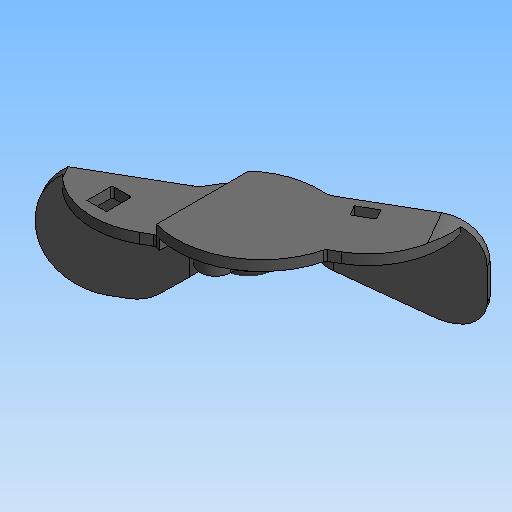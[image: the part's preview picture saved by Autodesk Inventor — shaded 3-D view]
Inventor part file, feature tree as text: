
AUTODESK INVENTOR PART (.ipt)
format: ipt  version: 2020 (Build 240168000, 168)  size: 249,344 bytes
history: native  units: mm (DEFAULTED — no unit token found)
features: sketch x7, other x7, extrude x6, revolve x1
ambient origin geometry x8: Origin, YZ Plane, XZ Plane, XY Plane, X Axis, Y Axis, Z Axis, Center Point
bodies: Solid1 (feature_tree)
feature tree (21):
  extrude  "Extrusion1"  Depth=50.0mm TaperAngle=0.0deg
  extrude  "Extrusion2"  Depth=2.3mm TaperAngle=0.0deg
  extrude  "Extrusion3"  Depth=2.7mm TaperAngle=0.0deg
  extrude  "Extrusion4"  TaperAngle=0.0deg  [1 undecoded]
  extrude  "Extrusion5"  [1 undecoded]
  sketch  "Sketch_7"
  extrude  "Extrusion6"  [1 undecoded]
  revolve  "Revolution1"  [1 undecoded]
  other  "stopper_to_body_XY"
  other  "stopper_to_body_YZ"
  other  "stopper_to_body_ZX"
  other  "stopper_to_body_X"
  other  "stopper_to_body_Y"
  other  "stopper_to_body_Z"
  other  "stopper_to_body_Center"
  sketch  "Sketch_1"  dims[d0=25.0mm d1=0.0mm d2=50.0mm d3=0.0mm]
  sketch  "Sketch_2"  dims[d4=50.0mm d5=0.0mm d6=2.3mm d7=0.0mm]
  sketch  "Sketch_8"
  sketch  "Sketch_9"
  sketch  "Sketch_3"  dims[d8=100.0mm d9=0.0mm d10=2.7mm d11=0.0mm]
  sketch  "Sketch_4"  dims[d12=360.0deg d13=0.0mm]
note: 4 required parameter values undecoded (feature->parameter linkage not recoverable at this tier; creation-order binding heuristic only, values carry confidence <= 0.55)
